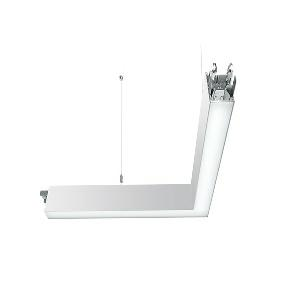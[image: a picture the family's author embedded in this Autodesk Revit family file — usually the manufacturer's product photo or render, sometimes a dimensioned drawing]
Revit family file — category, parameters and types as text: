
# Revit family: idoo_line_-_ilp_3000_830_d_ll_mid_00807702_24e8
name_source: partatom
category: Lighting Fixtures
units: mm (PartAtom-declared; Revit-internal decimal feet)

## family parameters
Cut with Voids When Loaded = No
Host = Face
Light Source = No
Part Type = Normal
Room Calculation Point = No
Round Connector Dimension = Use Diameter
Shared = No

## types (1)
- IDOO.line - ILP 3000/830/D/LL MID (1 x LED, 3000 lm, 3000K)
    Apparent Load = 23 VA
    Approval mark = CE
    CIE Flux Codes = 66 91 98 40 100
    Color Rendering = 80-89
    Color Temperature = 3000K
    Control Gear = Electronic ballast
    Default Elevation = 1800 mm
    Description = ILP 3000/830/D|Suspended luminaire|light source: LED|connected load: 220-240 V, 50/60 Hz|Power consumption: approx. 23 W|standby: approx. 0,20|luminous flux: 3000 lm|luminous efficacy: 130 lm/W|light distribution: Direct/indirect|direct ratio: approx. 40 %|colour temperature: Warm white, ca. 3000 K|color rendering index (CRI): >= 80|chromaticity tolerance:  3 SDCM|System of protection: IP 40|technology: Continuously dimmable|luminaire body|material: Sectional aluminium|colour: White|lamp cover: Acrylic (PMMA), Clear|Fastening: Steel cable 0.3 - 0.7 m|glare control: Prism aperture|luminance(L65): <= 2700 cd/m|unified glare rating(4H 8H): <=  16|special features: DALI Load 1x, TouchDIM - dimming via standard switch, Through-wired, up to 18 m on one mains connection, Flicker-free, Continous light without dark z, 90░ rerouting on the left side, Suitable as emergency lighting, Mechanical and electrical connection of the individual modules without tools|
    Frequency = 50 Hz
    Height = 110 mm
    Lamp = 1 x LED
    Lamp Light Flux = 3000 lm
    Lamp count = 1
    Length = 600 mm
    Luminous efficacy = 130 lm/W
    Manufacturer = Waldmann
    ModVariant = No
    Model = 00807702
    Mounting Place = Ceiling
    Mounting Type = Pendant
    Number of Poles = 1
    OnlyDefault = Yes
    Power Factor = 1
    Product Name = IDOO.line - ILP 3000/830/D/LL MID
    Product group = Suspended luminaire
    ProductGroupID = 9
    Protection Class = Protection class I
    Protection Degree = IP 40
    RLX_Detail_Level = 1
    RLX_Emergency_Light_Flux = 0 lm
    RLX_Emergency_Type = 0
    RLX_Emergency_Type_DB = No
    RlxData = <blob elided: 20925 chars, md5=198dcf6b>
    Socket = socket
    Standby Power = 0 W
    System Light Flux = 3000 lm
    System Power = 23 W
    Type Comments = Product without accessories
    Type Image = ilp_dlp_ll_ws.jpg
    URL = http://relux.com
    VarID = ---
    Voltage = 230 V
    Voltage Range = 220-240 V
    Weight = 0.00 kg
    Width = 600 mm

## geometry (parser evidence)
native form markers: Blend x4, Sweep x12
no freeform markers — native parametric forms only
